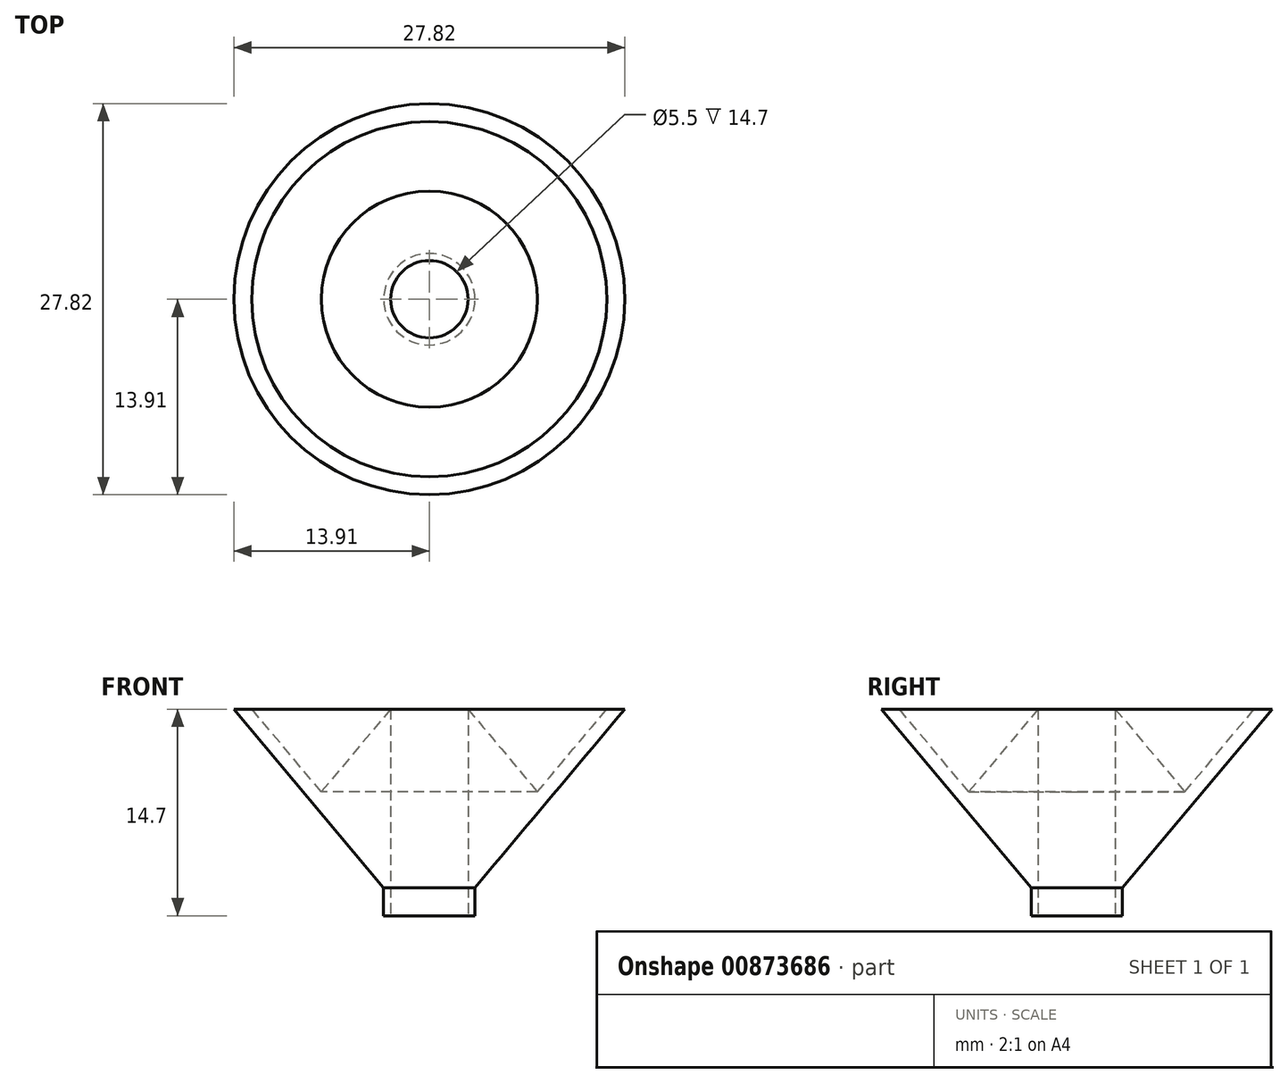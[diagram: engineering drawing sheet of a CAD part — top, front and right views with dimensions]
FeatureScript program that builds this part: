
annotation { "Feature Type Name" : "Feature", "Feature Type Description" : "" }
export const myFeature = defineFeature(function(context is Context, id is Id, definition is map)
    precondition{}
    {
        {
            var Q0;
            Q0=qCreatedBy(makeId("Top.planeOp"),FACE);
            var sketch = newSketch(context, id + "F0", { "sketchPlane" : qUnion([Q0])});
            skCircle(sketch, "E0", {"center": v(0, 0) * mm, "radius": 2.75 * mm});
            skCircle(sketch, "E1", {"center": v(0, 0) * mm, "radius": 3.25 * mm});
            skSolve(sketch);
        }
        {
            var Q0;
            Q0=makeQuery(id+"F0.imprint","IMPRINT",FACE,{"disambiguationData":[TD([[makeQuery(id+"F0.imprint","IMPRINT",EDGE,{"derivedFrom":sQuery(id+"F0.wireOp",EDGE,"E0")}),-1.0]])]});
            extrude(context, id + "F1", {"entities" : qUnion([Q0]), "depth" : 2 * mm, "offsetDistance" : 25.4 * mm});
        }
        {
            var Q0;
            Q0=makeQuery(id+"F1.opExtrude","CAP_FACE",FACE,{"disambiguationData":[OSD([sQuery(id+"F0.wireOp",EDGE,"E0"),sQuery(id+"F0.wireOp",EDGE,"E1")])],"isStart":false});
            extrude(context, id + "F2", {"entities" : qUnion([Q0]), "operationType" : NewBodyOperationType.ADD, "depth" : 12.7 * mm, "offsetDistance" : 25.4 * mm, "hasDraft" : true, "draftAngle" : 40 * degree});
        }
        {
            var Q0;
            Q0=makeQuery(id+"F2.opExtrude","CAP_FACE",FACE,{"disambiguationData":[OSD([sQuery(id+"F0.wireOp",EDGE,"E0"),sQuery(id+"F0.wireOp",EDGE,"E1")])],"isStart":false});
            var sketch = newSketch(context, id + "F3", { "sketchPlane" : qUnion([Q0])});
            skCircle(sketch, "E2", {"center": v(0, 0) * mm, "radius": 2.75 * mm});
            skSolve(sketch);
        }
        {
            var Q0;
            Q0 = qSketchRegion(id + "F3", true);
            extrude(context, id + "F4", {"entities" : qUnion([Q0]), "operationType" : NewBodyOperationType.REMOVE, "endBound" : BoundingType.UP_TO_NEXT, "oppositeDirection" : true, "depth" : 25.4 * mm, "offsetDistance" : 25.4 * mm});
        }
        {
            var Q0;
            Q0=makeQuery(id+"F2.opExtrude","CAP_FACE",FACE,{"disambiguationData":[OSD([sQuery(id+"F0.wireOp",EDGE,"E0"),sQuery(id+"F0.wireOp",EDGE,"E1")])],"isStart":false});
            var sketch = newSketch(context, id + "F5", { "sketchPlane" : qUnion([Q0])});
            skCircle(sketch, "E3", {"center": v(0, 0) * mm, "radius": 12.63 * mm});
            skSolve(sketch);
        }
        {
            var Q0;
            Q0=makeQuery(id+"F5.imprint","IMPRINT",FACE,{"disambiguationData":[TD([[makeQuery(id+"F5.imprint","IMPRINT",EDGE,{"derivedFrom":sQuery(id+"F5.wireOp",EDGE,"E3")}),1.0]])]});
            extrude(context, id + "F6", {"entities" : qUnion([Q0]), "operationType" : NewBodyOperationType.REMOVE, "oppositeDirection" : true, "depth" : 13.8 * mm, "offsetDistance" : 25.4 * mm, "hasDraft" : true, "draftAngle" : 40 * degree, "draftPullDirection" : true});
        }
    });
